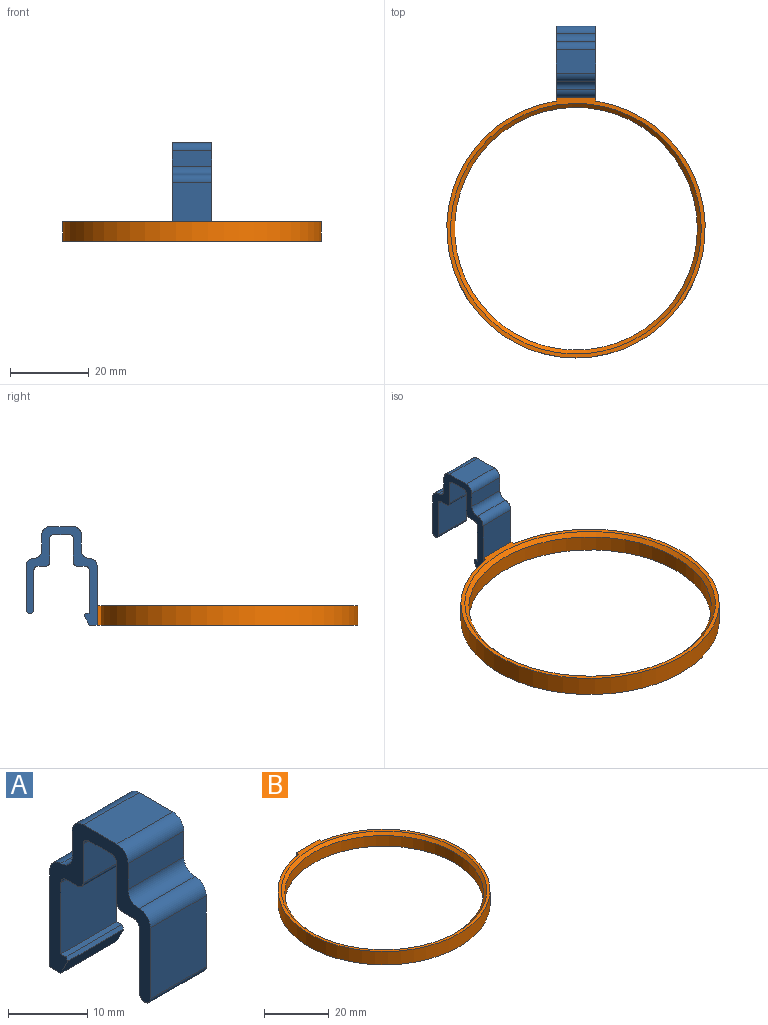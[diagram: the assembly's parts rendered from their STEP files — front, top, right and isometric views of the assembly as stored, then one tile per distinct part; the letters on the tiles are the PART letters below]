
ASSEMBLY  parts=2 mates=1
PART A: 31 faces, bbox 10x18x25 mm
  f0: plane 10x10mm, normal (0,1,0), area 100mm2, adj f15,f16,f23,f29
  f1: plane 10x2mm, normal (0,0,-1), area 20mm2, adj f15,f16,f23,f24
  f2: plane 10x6mm, normal (0,1,0), area 60mm2, adj f15,f16,f24,f25
  f3: plane 10x4mm, normal (0,0,-1), area 40mm2, adj f15,f16,f25,f26
  f4: plane 10x6mm, normal (0,-1,0), area 60mm2, adj f15,f16,f26,f27
  f5: plane 10x2mm, normal (0,0,-1), area 20mm2, adj f15,f16,f27,f28
  f6: plane 11x10mm, normal (0,-1,0), area 110mm2, adj f7,f15,f16,f28
  f7: plane 10x0.9mm, normal (0,0,1), area 9mm2, adj f6,f15,f16,f30
  f8: plane 10x2.46mm, normal (0,-0.89,-0.45), area 27.5mm2, adj f9,f15,f16,f30
  f9: plane 10x2mm, normal (0,0,-1), area 20mm2, adj f8,f10,f15,f16
  f10: plane 15x10mm, normal (0,1,0), area 150mm2, adj f9,f15,f16,f18
  f11: plane 10x4mm, normal (0,1,0), area 40mm2, adj f15,f16,f17,f19
  f12: plane 10x6mm, normal (0,0,1), area 60mm2, adj f15,f16,f19,f20
  f13: plane 10x4mm, normal (0,-1,0), area 40mm2, adj f15,f16,f20,f22
  f14: plane 11x10mm, normal (0,-1,0), area 110mm2, adj f15,f16,f21,f29
  f15: plane 25x18mm, normal (1,0,0), area 122.4mm2, adj f0,f1,f2,f3,f4,f5,f6,f7
  f16: plane 25x18mm, normal (-1,0,0), area 122.4mm2, adj f0,f1,f2,f3,f4,f5,f6,f7
  f17: cylinder r=2mm len=10mm, axis (1,0,0), area 31.4mm2, adj f11,f15,f16,f18
  f18: cylinder r=2mm len=10mm, axis (-1,0,0), area 31.4mm2, adj f10,f15,f16,f17
  f19: cylinder r=2mm len=10mm, axis (-1,0,0), area 31.4mm2, adj f11,f12,f15,f16
  f20: cylinder r=2mm len=10mm, axis (1,0,0), area 31.4mm2, adj f12,f13,f15,f16
  f21: cylinder r=2mm len=10mm, axis (-1,0,0), area 31.4mm2, adj f14,f15,f16,f22
  f22: cylinder r=2mm len=10mm, axis (1,0,0), area 31.4mm2, adj f13,f15,f16,f21
  f23: cylinder r=1mm len=10mm, axis (1,0,0), area 15.7mm2, adj f0,f1,f15,f16
  f24: cylinder r=1mm len=10mm, axis (-1,0,0), area 15.7mm2, adj f1,f2,f15,f16
  f25: cylinder r=1mm len=10mm, axis (-1,0,0), area 15.7mm2, adj f2,f3,f15,f16
  f26: cylinder r=1mm len=10mm, axis (1,0,0), area 15.7mm2, adj f3,f4,f15,f16
  f27: cylinder r=1mm len=10mm, axis (-1,0,0), area 15.7mm2, adj f4,f5,f15,f16
  f28: cylinder r=1mm len=10mm, axis (1,0,0), area 15.7mm2, adj f5,f6,f15,f16
  f29: cylinder r=1mm len=10mm, axis (1,0,0), area 31.4mm2, adj f0,f14,f15,f16
  f30: plane 10x0.54mm, normal (0,-0.85,0.53), area 6.3mm2, adj f7,f8,f15,f16
PART B: 8 faces, bbox 65.5x66.1x5 mm
  f0: plane 10x5mm, normal (0,1,0), area 50mm2, adj f1,f3,f5,f6
  f1: plane 5x1mm, normal (-1,0,0), area 5mm2, adj f0,f2,f5,f6
  f2: cylinder r=32.75mm len=65.5mm, axis (0,0,-1), area 978.7mm2, adj f1,f3,f5,f6
  f3: plane 5x1mm, normal (1,0,0), area 5mm2, adj f0,f2,f5,f6
  f4: cylinder r=30.75mm len=61.5mm, axis (0,0,-1), area 772.8mm2, adj f6,f7
  f5: plane 66.12x65.5mm, normal (0,0,1), area 210.1mm2, adj f0,f1,f2,f3,f7
  f6: plane 66.12x65.5mm, normal (0,0,-1), area 406.4mm2, adj f0,f1,f2,f3,f4
  f7: cone r=30.75mm half-angle=45deg, axis (0,0,1), area 277.7mm2, adj f4,f5
PLACE A rot(axis=(0,0,1),180deg) t=(-10.95,36.21,-5.41)mm
PLACE B t=(-15.95,-13.15,-8.41)mm
MATE fastened A.f10 <-> B.f0  axis (0,-1,0) through (-15.95,20.21,-8.41)mm
